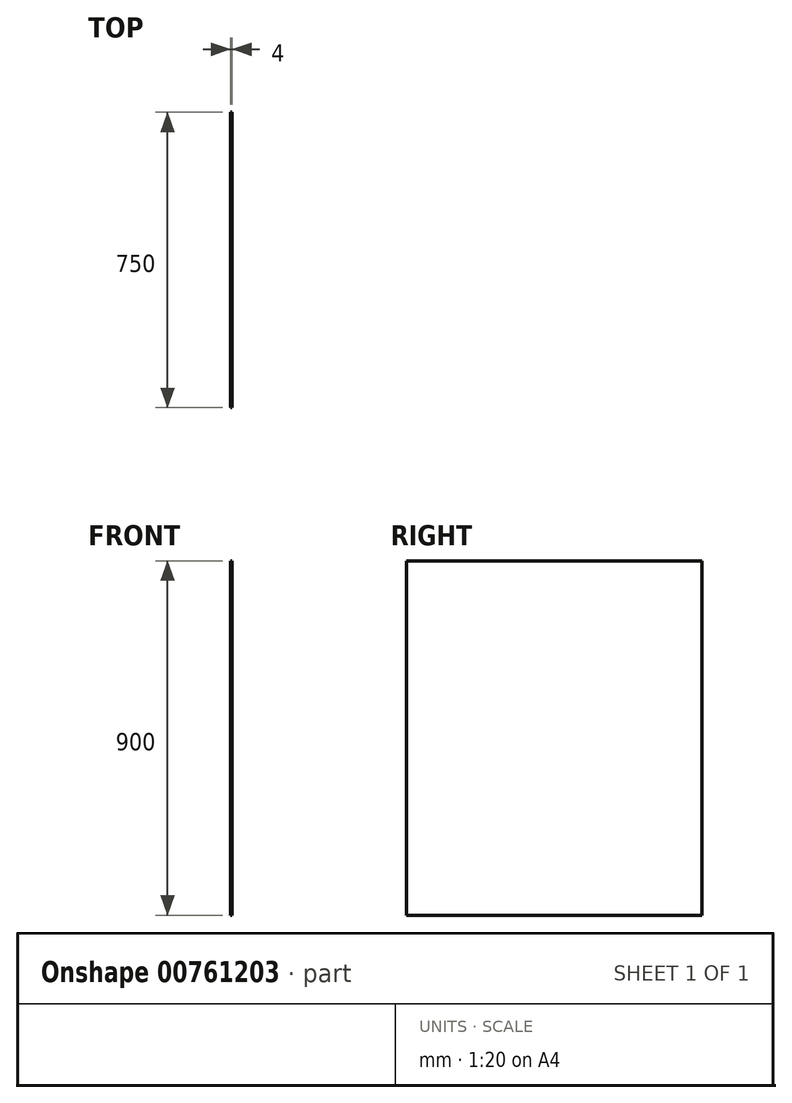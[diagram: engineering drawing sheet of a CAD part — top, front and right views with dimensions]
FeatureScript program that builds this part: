
annotation { "Feature Type Name" : "Feature", "Feature Type Description" : "" }
export const myFeature = defineFeature(function(context is Context, id is Id, definition is map)
    precondition{}
    {
        {
            var Q0;
            Q0=qCreatedBy(makeId("Right.planeOp"),FACE);
            var sketch = newSketch(context, id + "F0", { "sketchPlane" : qUnion([Q0])});
            skLineSegment(sketch, "E0.bottom", {"start": v(0, 0) * mm, "end": v(750, 0) * mm});
            skLineSegment(sketch, "E0.top", {"start": v(0, 900) * mm, "end": v(750, 900) * mm});
            skLineSegment(sketch, "E0.left", {"start": v(0, 0) * mm, "end": v(0, 900) * mm});
            skLineSegment(sketch, "E0.right", {"start": v(750, 0) * mm, "end": v(750, 900) * mm});
            skSolve(sketch);
        }
        {
            var Q0;
            Q0 = qSketchRegion(id + "F0", true);
            extrude(context, id + "F1", {"entities" : qUnion([Q0]), "depth" : 4 * mm, "offsetDistance" : 25 * mm});
        }
    });
